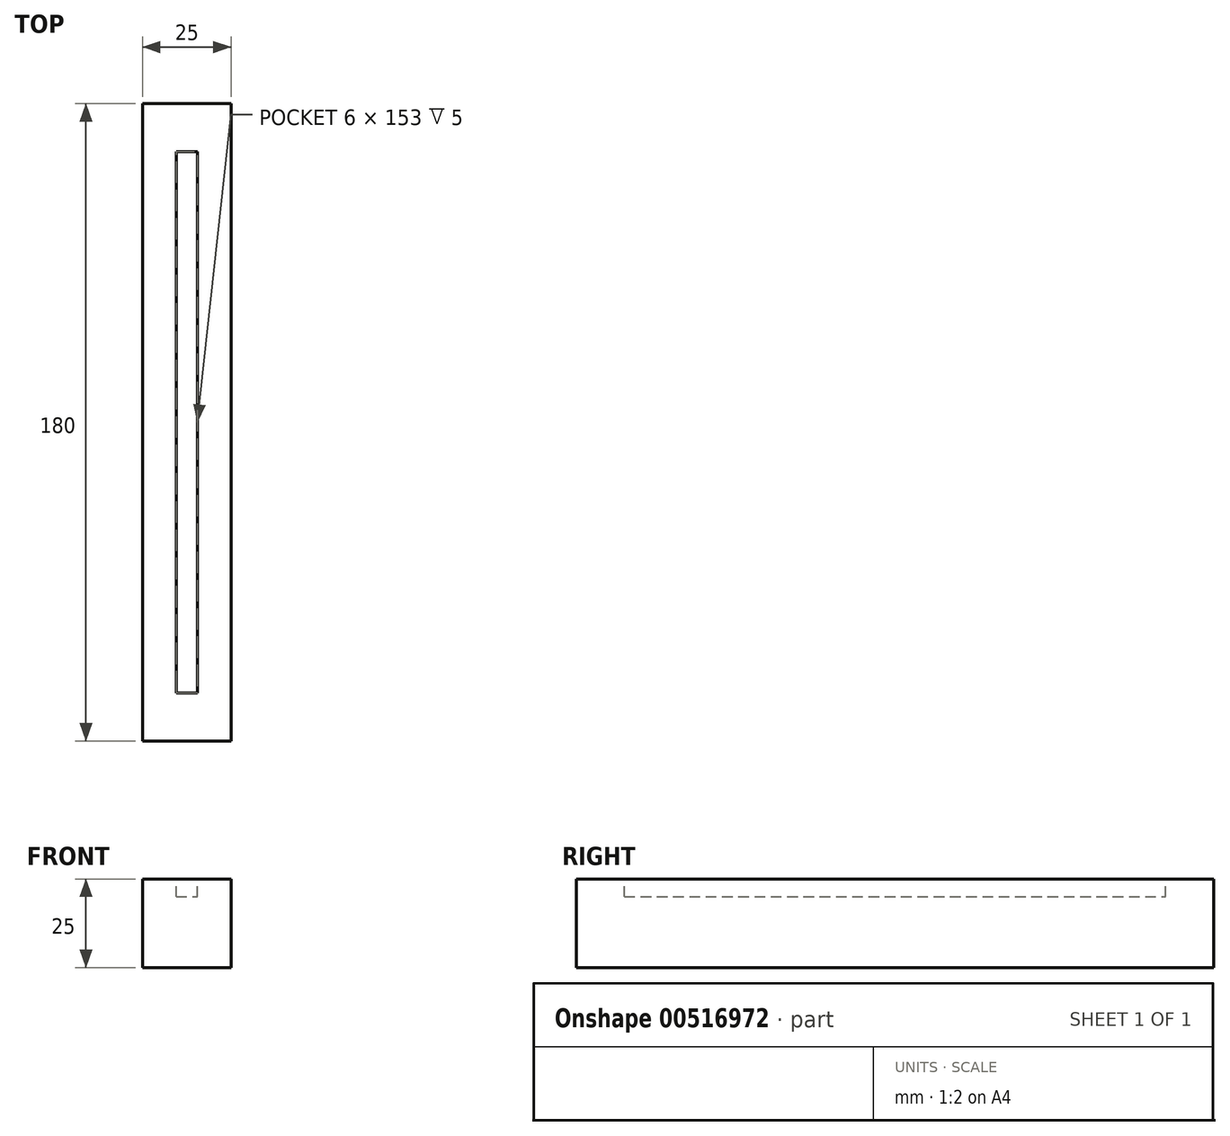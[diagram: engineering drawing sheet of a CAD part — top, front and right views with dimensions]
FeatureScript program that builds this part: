
annotation { "Feature Type Name" : "Feature", "Feature Type Description" : "" }
export const myFeature = defineFeature(function(context is Context, id is Id, definition is map)
    precondition{}
    {
        {
            var Q0;
            Q0=qCreatedBy(makeId("Top.planeOp"),FACE);
            var sketch = newSketch(context, id + "F0", { "sketchPlane" : qUnion([Q0])});
            skLineSegment(sketch, "E0.bottom", {"start": v(-12.5, -90) * mm, "end": v(12.5, -90) * mm});
            skLineSegment(sketch, "E0.top", {"start": v(-12.5, 90) * mm, "end": v(12.5, 90) * mm});
            skLineSegment(sketch, "E0.left", {"start": v(-12.5, -90) * mm, "end": v(-12.5, 90) * mm});
            skLineSegment(sketch, "E0.right", {"start": v(12.5, -90) * mm, "end": v(12.5, 90) * mm});
            skPoint(sketch, "E1", {"position": v(0, -90) * mm});
            skPoint(sketch, "E2", {"position": v(12.5, 0) * mm});
            skSolve(sketch);
        }
        {
            var Q0;
            Q0=makeQuery(id+"F0.imprint","IMPRINT",FACE,{"disambiguationData":[TD([[makeQuery(id+"F0.imprint","IMPRINT",EDGE,{"derivedFrom":sQuery(id+"F0.wireOp",EDGE,"E0.bottom")}),1.0]])]});
            extrude(context, id + "F1", {"entities" : qUnion([Q0]), "depth" : 25 * mm, "offsetDistance" : 25 * mm});
        }
        {
            var Q0;
            Q0=makeQuery(id+"F1.opExtrude","CAP_FACE",FACE,{"disambiguationData":[OSD([sQuery(id+"F0.wireOp",EDGE,"E0.bottom"),sQuery(id+"F0.wireOp",EDGE,"E0.top"),sQuery(id+"F0.wireOp",EDGE,"E0.left"),sQuery(id+"F0.wireOp",EDGE,"E0.right")])],"isStart":false});
            var sketch = newSketch(context, id + "F2", { "sketchPlane" : qUnion([Q0])});
            skLineSegment(sketch, "E3.bottom", {"start": v(-3, -76.5) * mm, "end": v(3, -76.5) * mm});
            skLineSegment(sketch, "E3.top", {"start": v(-3, 76.5) * mm, "end": v(3, 76.5) * mm});
            skLineSegment(sketch, "E3.left", {"start": v(-3, -76.5) * mm, "end": v(-3, 76.5) * mm});
            skLineSegment(sketch, "E3.right", {"start": v(3, -76.5) * mm, "end": v(3, 76.5) * mm});
            skPoint(sketch, "E4.positionSnap0", {"position": v(0, -90) * mm});
            skPoint(sketch, "E5", {"position": v(-3, 0) * mm});
            skPoint(sketch, "E6", {"position": v(0, -76.5) * mm});
            skSolve(sketch);
        }
        {
            var Q0;
            Q0=makeQuery(id+"F2.imprint","IMPRINT",FACE,{"disambiguationData":[TD([[makeQuery(id+"F2.imprint","IMPRINT",EDGE,{"derivedFrom":sQuery(id+"F2.wireOp",EDGE,"E3.bottom")}),1.0]])]});
            extrude(context, id + "F3", {"entities" : qUnion([Q0]), "operationType" : NewBodyOperationType.REMOVE, "oppositeDirection" : true, "depth" : 5 * mm, "offsetDistance" : 25 * mm});
        }
    });
